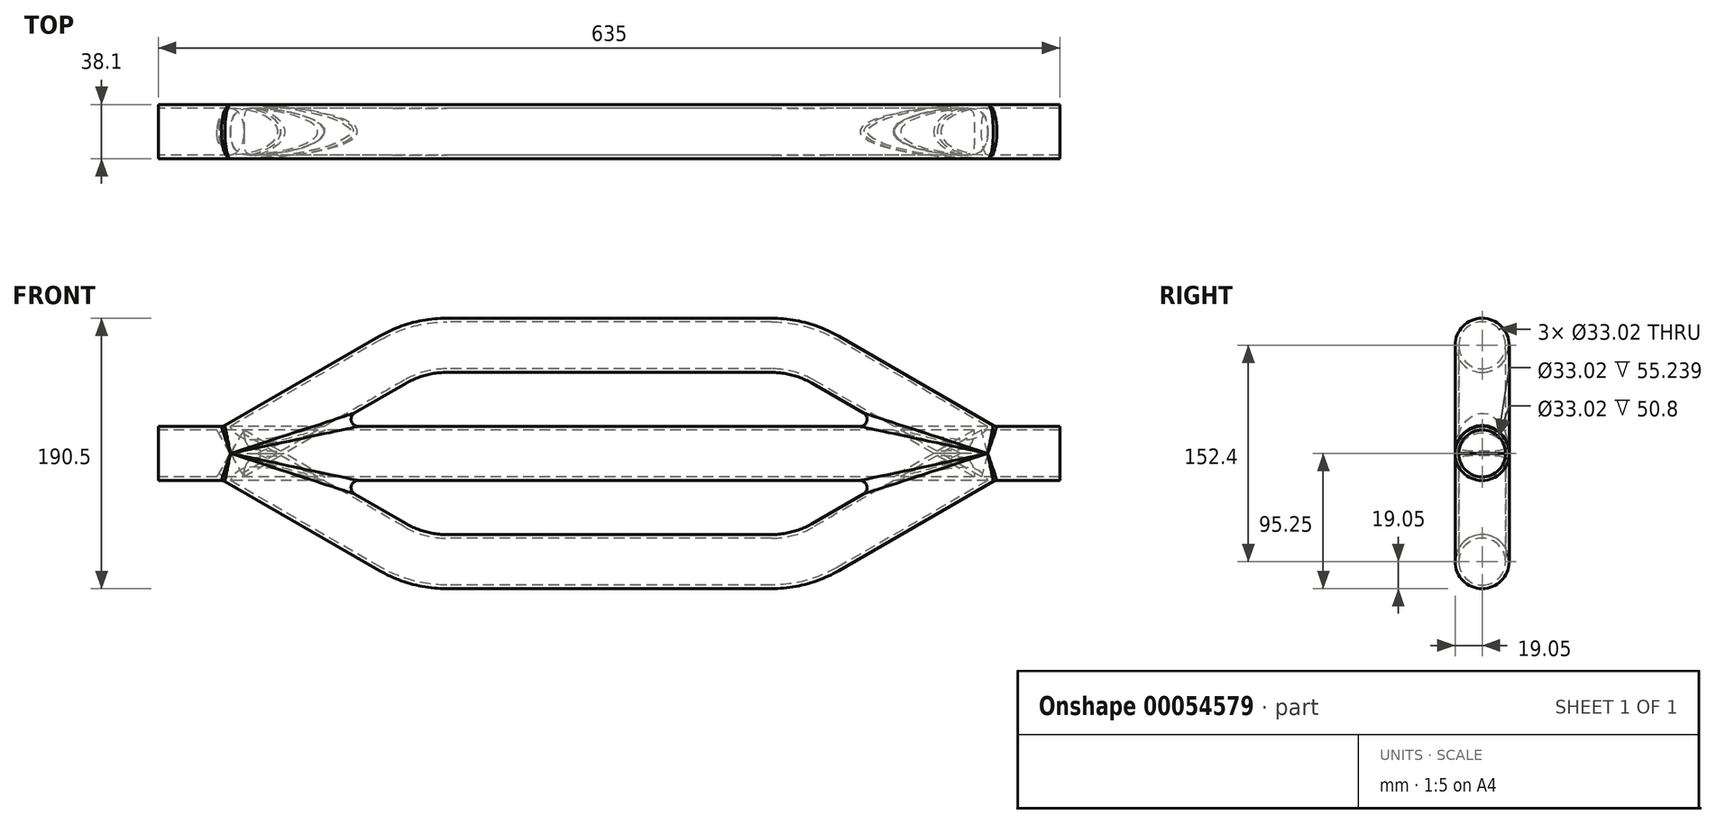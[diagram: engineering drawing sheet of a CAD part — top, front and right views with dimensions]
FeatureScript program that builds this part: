
annotation { "Feature Type Name" : "Feature", "Feature Type Description" : "" }
export const myFeature = defineFeature(function(context is Context, id is Id, definition is map)
    precondition{}
    {
        {
            var Q0;
            Q0=qCreatedBy(makeId("Right.planeOp"),FACE);
            var sketch = newSketch(context, id + "F0", { "sketchPlane" : qUnion([Q0])});
            skCircle(sketch, "E0", {"center": v(0, 0) * mm, "radius": 19.05 * mm});
            skCircle(sketch, "E1", {"center": v(0, 0) * mm, "radius": 16.51 * mm});
            skSolve(sketch);
        }
        {
            var Q0;
            Q0=qCreatedBy(makeId("Front.planeOp"),FACE);
            var sketch = newSketch(context, id + "F1", { "sketchPlane" : qUnion([Q0])});
            skLineSegment(sketch, "E2", {"start": v(0, 0) * mm, "end": v(-635, 0) * mm});
            skSolve(sketch);
        }
        {
            var Q0;
            Q0=qCreatedBy(makeId("Front.planeOp"),FACE);
            var sketch = newSketch(context, id + "F2", { "sketchPlane" : qUnion([Q0])});
            skLineSegment(sketch, "E3", {"start": v(-50.8, 0) * mm, "end": v(-165.1, 66) * mm});
            skLineSegment(sketch, "E4", {"start": v(-203.2, 76.2) * mm, "end": v(-431.8, 76.2) * mm});
            skLineSegment(sketch, "E5", {"start": v(-469.9, 66) * mm, "end": v(-584.2, 0) * mm});
            skLineSegment(sketch, "E6", {"start": v(-50.8, 0) * mm, "end": v(0, 0) * mm});
            skPoint(sketch, "E7.visualSharp", {"position": v(-452.22, 76.2) * mm});
            skArc(sketch, "E7.filletArc", {"start": v(-431.8, 76.2) * mm, "mid": v(-451.52, 73.6) * mm, "end": v(-469.9, 66) * mm});
            skPoint(sketch, "E8.visualSharp", {"position": v(-182.78, 76.2) * mm});
            skArc(sketch, "E8.filletArc", {"start": v(-165.1, 66) * mm, "mid": v(-183.48, 73.6) * mm, "end": v(-203.2, 76.2) * mm});
            skSolve(sketch);
        }
        {
            var Q0;
            Q0=qCreatedBy(makeId("Front.planeOp"),FACE);
            var sketch = newSketch(context, id + "F3", { "sketchPlane" : qUnion([Q0])});
            skLineSegment(sketch, "E9", {"start": v(-50.8, 0) * mm, "end": v(-165.1, -66) * mm});
            skLineSegment(sketch, "E10", {"start": v(-203.2, -76.2) * mm, "end": v(-431.8, -76.2) * mm});
            skLineSegment(sketch, "E11", {"start": v(-469.9, -66) * mm, "end": v(-584.2, 0) * mm});
            skLineSegment(sketch, "E12", {"start": v(-50.8, 0) * mm, "end": v(0, 0) * mm});
            skPoint(sketch, "E13.visualSharp", {"position": v(-452.22, -76.2) * mm});
            skArc(sketch, "E13.filletArc", {"start": v(-469.9, -66) * mm, "mid": v(-451.52, -73.6) * mm, "end": v(-431.8, -76.2) * mm});
            skPoint(sketch, "E14.visualSharp", {"position": v(-182.78, -76.2) * mm});
            skArc(sketch, "E14.filletArc", {"start": v(-203.2, -76.2) * mm, "mid": v(-183.48, -73.6) * mm, "end": v(-165.1, -66) * mm});
            skSolve(sketch);
        }
        {
            var Q0;
            Q0 = qSketchRegion(id + "F0", true);
            var Q1;
            Q1=sQuery(id+"F1.wireOp",EDGE,"E2");
            sweep(context, id + "F4", {"profiles" : qUnion([Q0]), "path" : qUnion([Q1])});
        }
        {
            var Q0;
            Q0 = qSketchRegion(id + "F0", true);
            var Q1;
            Q1 = qConstructionFilter(qBodyType(qCreatedBy(id + "F2" ,EDGE), BodyType.WIRE), ConstructionObject.NO);
            sweep(context, id + "F5", {"operationType" : NewBodyOperationType.ADD, "profiles" : qUnion([Q0]), "path" : qUnion([Q1])});
        }
        {
            var Q0;
            Q0 = qSketchRegion(id + "F0", true);
            var Q1;
            Q1 = qConstructionFilter(qBodyType(qCreatedBy(id + "F3" ,EDGE), BodyType.WIRE), ConstructionObject.NO);
            sweep(context, id + "F6", {"operationType" : NewBodyOperationType.ADD, "profiles" : qUnion([Q0]), "path" : qUnion([Q1])});
        }
        {
            var Q0;
            {var subQ0=sQuery(id+"F0.wireOp",EDGE,"E0");Q0=makeQuery(id+"F5.boolean.opBoolean","INTERSECT",EDGE,{"disambiguationData":[OD(1.0)],"derivedFrom":[makeQuery(id+"F4.opSweep","SWEPT_FACE",FACE,{"disambiguationData":[OSD([subQ0,sQuery(id+"F1.wireOp",EDGE,"E2")])]}),makeQuery(id+"F5.opSweep","SWEPT_FACE",FACE,{"disambiguationData":[OSD([subQ0,sQuery(id+"F2.wireOp",EDGE,"E5")])]})]});}
            var Q1;
            {var subQ0=sQuery(id+"F0.wireOp",EDGE,"E0");Q1=makeQuery(id+"F6.boolean.opBoolean","INTERSECT",EDGE,{"disambiguationData":[OD(1.0)],"derivedFrom":[makeQuery(id+"F5.boolean.opBoolean","SPLIT",FACE,{"disambiguationData":[TD([makeQuery(id+"F5.opSweep","SWEPT_FACE",FACE,{"disambiguationData":[OSD([subQ0,sQuery(id+"F2.wireOp",EDGE,"E3")])]})])],"derivedFrom":makeQuery(id+"F4.opSweep","SWEPT_FACE",FACE,{"disambiguationData":[OSD([subQ0,sQuery(id+"F1.wireOp",EDGE,"E2")])]})}),makeQuery(id+"F6.opSweep","SWEPT_FACE",FACE,{"disambiguationData":[OSD([subQ0,sQuery(id+"F3.wireOp",EDGE,"E11")])]})]});}
            var Q2;
            {var subQ0=sQuery(id+"F0.wireOp",EDGE,"E0");Q2=makeQuery(id+"F5.boolean.opBoolean","INTERSECT",EDGE,{"derivedFrom":[makeQuery(id+"F4.opSweep","SWEPT_FACE",FACE,{"disambiguationData":[OSD([subQ0,sQuery(id+"F1.wireOp",EDGE,"E2")])]}),makeQuery(id+"F5.opSweep","SWEPT_FACE",FACE,{"disambiguationData":[OSD([subQ0,sQuery(id+"F2.wireOp",EDGE,"E3")])]})]});}
            var Q3;
            {var subQ0=sQuery(id+"F0.wireOp",EDGE,"E0");Q3=makeQuery(id+"F6.boolean.opBoolean","INTERSECT",EDGE,{"derivedFrom":[makeQuery(id+"F5.boolean.opBoolean","SPLIT",FACE,{"disambiguationData":[TD([makeQuery(id+"F5.opSweep","SWEPT_FACE",FACE,{"disambiguationData":[OSD([subQ0,sQuery(id+"F2.wireOp",EDGE,"E3")])]})])],"derivedFrom":makeQuery(id+"F4.opSweep","SWEPT_FACE",FACE,{"disambiguationData":[OSD([subQ0,sQuery(id+"F1.wireOp",EDGE,"E2")])]})}),makeQuery(id+"F6.opSweep","SWEPT_FACE",FACE,{"disambiguationData":[OSD([subQ0,sQuery(id+"F3.wireOp",EDGE,"E9")])]})]});}
            var Q4;
            Q4=makeQuery(id+"F5.opSweep","MID_CAP_EDGE",EDGE,{"disambiguationData":[OSD([sQuery(id+"F0.wireOp",EDGE,"E0"),sQuery(id+"F2.wireOp",VERTEX,"E6.start")])],"capPos":1.0});
            var Q5;
            Q5=makeQuery(id+"F6.opSweep","MID_CAP_EDGE",EDGE,{"disambiguationData":[OSD([sQuery(id+"F0.wireOp",EDGE,"E0"),sQuery(id+"F3.wireOp",VERTEX,"E12.start")])],"capPos":1.0});
            var Q6;
            {var subQ0=sQuery(id+"F0.wireOp",EDGE,"E0");Q6=makeQuery(id+"F5.boolean.opBoolean","INTERSECT",EDGE,{"disambiguationData":[OD(0.0)],"derivedFrom":[makeQuery(id+"F4.opSweep","SWEPT_FACE",FACE,{"disambiguationData":[OSD([subQ0,sQuery(id+"F1.wireOp",EDGE,"E2")])]}),makeQuery(id+"F5.opSweep","SWEPT_FACE",FACE,{"disambiguationData":[OSD([subQ0,sQuery(id+"F2.wireOp",EDGE,"E5")])]})]});}
            var Q7;
            {var subQ0=sQuery(id+"F0.wireOp",EDGE,"E0");Q7=makeQuery(id+"F6.boolean.opBoolean","INTERSECT",EDGE,{"disambiguationData":[OD(0.0)],"derivedFrom":[makeQuery(id+"F5.boolean.opBoolean","SPLIT",FACE,{"disambiguationData":[TD([makeQuery(id+"F5.opSweep","SWEPT_FACE",FACE,{"disambiguationData":[OSD([subQ0,sQuery(id+"F2.wireOp",EDGE,"E3")])]})])],"derivedFrom":makeQuery(id+"F4.opSweep","SWEPT_FACE",FACE,{"disambiguationData":[OSD([subQ0,sQuery(id+"F1.wireOp",EDGE,"E2")])]})}),makeQuery(id+"F6.opSweep","SWEPT_FACE",FACE,{"disambiguationData":[OSD([subQ0,sQuery(id+"F3.wireOp",EDGE,"E11")])]})]});}
            fillet(context, id + "F7", {"entities" : qUnion([Q0, Q1, Q2, Q3, Q4, Q5, Q6, Q7]), "radius" : 5.08 * mm, "tangentPropagation" : true, "allowEdgeOverflow" : false});
        }
    });
